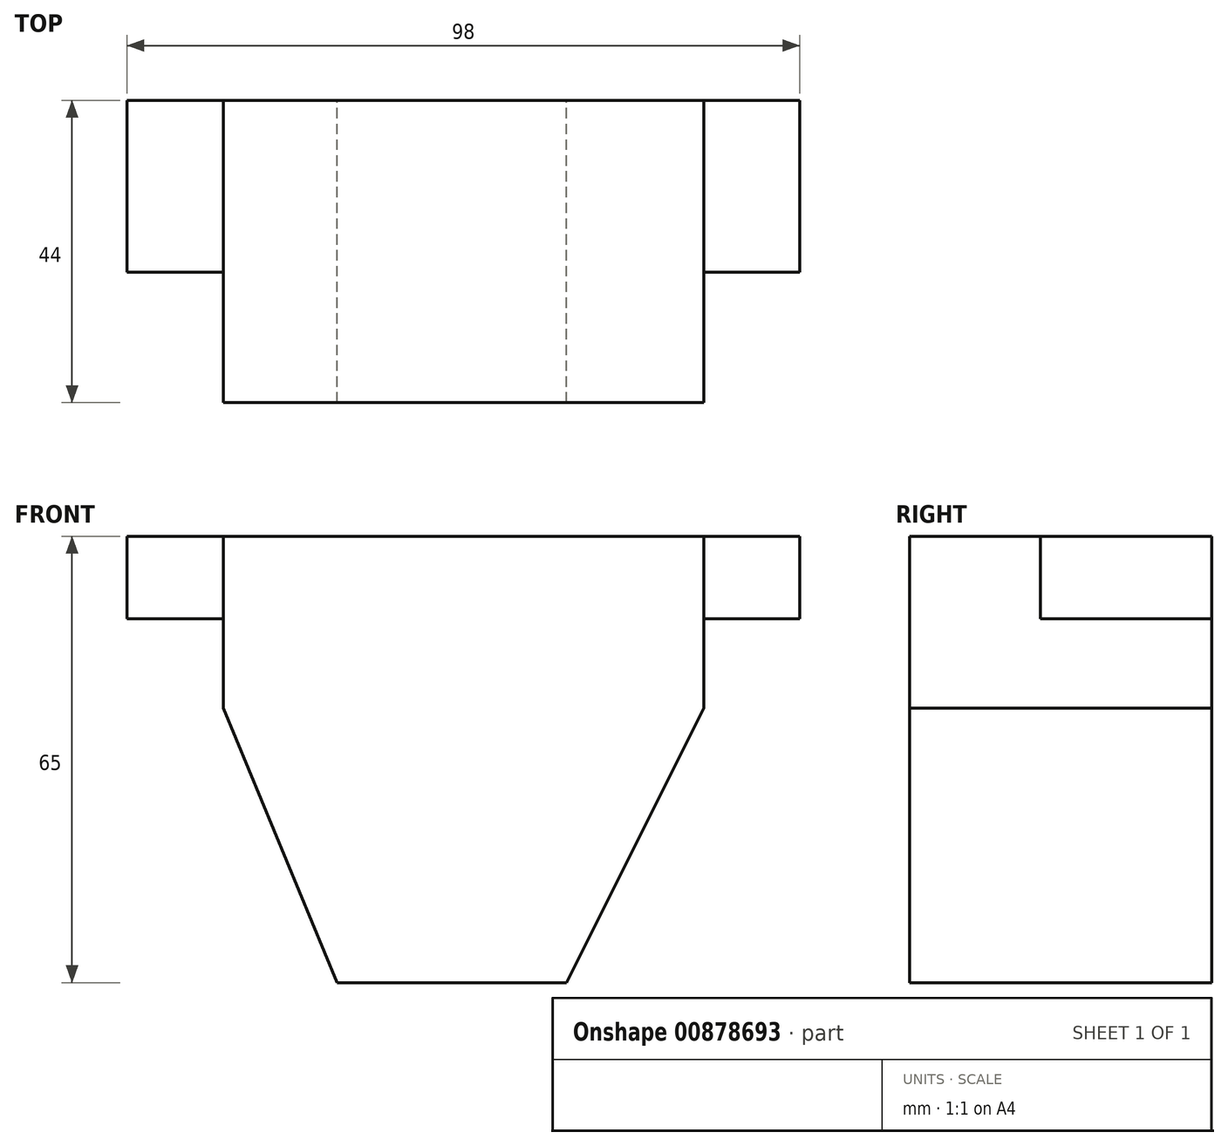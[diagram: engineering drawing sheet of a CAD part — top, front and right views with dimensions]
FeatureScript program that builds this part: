
annotation { "Feature Type Name" : "Feature", "Feature Type Description" : "" }
export const myFeature = defineFeature(function(context is Context, id is Id, definition is map)
    precondition{}
    {
        {
            var Q0;
            Q0=qCreatedBy(makeId("Front.planeOp"),FACE);
            var sketch = newSketch(context, id + "F0", { "sketchPlane" : qUnion([Q0])});
            skLineSegment(sketch, "E0.bottom", {"start": v(35, 32.5) * mm, "end": v(-35, 32.5) * mm});
            skLineSegment(sketch, "E0.top", {"start": v(15, -32.5) * mm, "end": v(-18.42, -32.5) * mm});
            skLineSegment(sketch, "E0.left", {"start": v(35, 32.5) * mm, "end": v(35, 7.5) * mm});
            skLineSegment(sketch, "E0.right", {"start": v(-35, 32.5) * mm, "end": v(-35, 7.5) * mm});
            skPoint(sketch, "E0.middle", {"position": v(0, 0) * mm});
            skLineSegment(sketch, "E1", {"start": v(-18.42, -32.5) * mm, "end": v(-35, 7.5) * mm});
            skLineSegment(sketch, "E2", {"start": v(15, -32.5) * mm, "end": v(35, 7.5) * mm});
            skPoint(sketch, "E3.start.orphan", {"position": v(-35, -32.5) * mm});
            skPoint(sketch, "E4.orphan", {"position": v(35, -32.5) * mm});
            skLineSegment(sketch, "E5.left", {"start": v(-35, 20.5) * mm, "end": v(-35, 32.5) * mm});
            skLineSegment(sketch, "E6.left", {"start": v(35, 32.5) * mm, "end": v(35, 20.5) * mm});
            skPoint(sketch, "E5.top.end.orphan", {"position": v(-49, 32.5) * mm});
            skLineSegment(sketch, "E7.left", {"start": v(-35, 32.5) * mm, "end": v(-35, 20.5) * mm});
            skPoint(sketch, "E7.top.end.orphan", {"position": v(-49, 20.5) * mm});
            skSolve(sketch);
        }
        {
            var Q0;
            {var subQ1=sQuery(id+"F0.wireOp",EDGE,"E0.bottom");Q0=makeQuery(id+"F0.imprint","IMPRINT",FACE,{"disambiguationData":[TD([[makeQuery(id+"F0.imprint","IMPRINT",EDGE,{"derivedFrom":subQ1}),1.0]])]});}
            extrude(context, id + "F1", {"entities" : qUnion([Q0]), "depth" : 44 * mm, "offsetDistance" : 25 * mm});
        }
        {
            var Q0;
            Q0=makeQuery(id+"F1.opExtrude","SWEPT_FACE",FACE,{"disambiguationData":[OSD([sQuery(id+"F0.wireOp",EDGE,"E0.bottom")])]});
            var sketch = newSketch(context, id + "F2", { "sketchPlane" : qUnion([Q0])});
            skLineSegment(sketch, "E8.bottom", {"start": v(35, 0) * mm, "end": v(49, 0) * mm});
            skLineSegment(sketch, "E8.top", {"start": v(35, -25) * mm, "end": v(49, -25) * mm});
            skLineSegment(sketch, "E8.left", {"start": v(35, 0) * mm, "end": v(35, -25) * mm});
            skLineSegment(sketch, "E8.right", {"start": v(49, 0) * mm, "end": v(49, -25) * mm});
            skLineSegment(sketch, "E9.bottom", {"start": v(-35, 0) * mm, "end": v(-49, 0) * mm});
            skLineSegment(sketch, "E9.top", {"start": v(-35, -25) * mm, "end": v(-49, -25) * mm});
            skLineSegment(sketch, "E9.left", {"start": v(-35, 0) * mm, "end": v(-35, -25) * mm});
            skLineSegment(sketch, "E9.right", {"start": v(-49, 0) * mm, "end": v(-49, -25) * mm});
            skSolve(sketch);
        }
        {
            var Q0;
            Q0=makeQuery(id+"F2.imprint","IMPRINT",FACE,{"disambiguationData":[TD([[makeQuery(id+"F2.imprint","IMPRINT",EDGE,{"derivedFrom":sQuery(id+"F2.wireOp",EDGE,"E9.bottom")}),1.0]])]});
            var Q1;
            Q1=makeQuery(id+"F2.imprint","IMPRINT",FACE,{"disambiguationData":[TD([[makeQuery(id+"F2.imprint","IMPRINT",EDGE,{"derivedFrom":sQuery(id+"F2.wireOp",EDGE,"E8.bottom")}),-1.0]])]});
            extrude(context, id + "F3", {"entities" : qUnion([Q0, Q1]), "oppositeDirection" : true, "depth" : 12 * mm, "offsetDistance" : 25 * mm});
        }
    });
